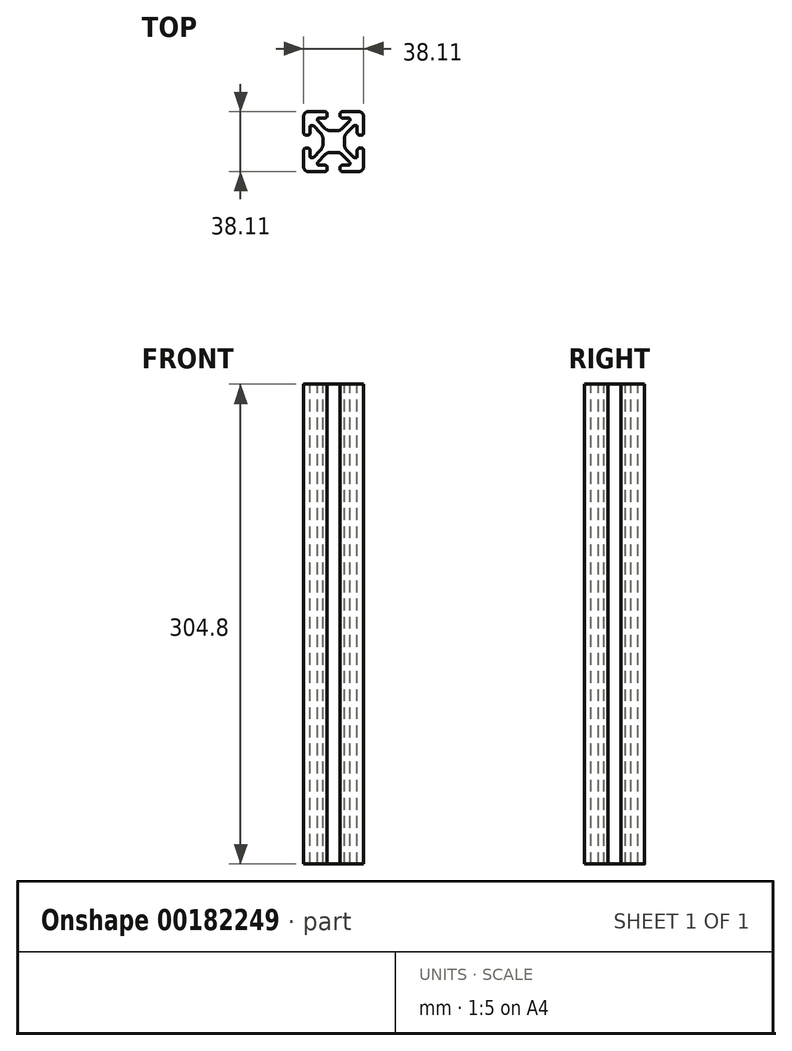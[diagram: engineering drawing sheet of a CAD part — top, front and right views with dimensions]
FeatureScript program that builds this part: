
annotation { "Feature Type Name" : "Feature", "Feature Type Description" : "" }
export const myFeature = defineFeature(function(context is Context, id is Id, definition is map)
    precondition{}
    {
        {
            var Q0;
            Q0=qCreatedBy(makeId("Top.planeOp"),FACE);
            var sketch = newSketch(context, id + "F0", { "sketchPlane" : qUnion([Q0])});
            skLineSegment(sketch, "E0.0", {"start": v(-3.18, 31.75) * mm, "end": v(-3.18, 21.51) * mm});
            skArc(sketch, "E1.0", {"start": v(0, 34.93) * mm, "mid": v(-2.25, 34) * mm, "end": v(-3.18, 31.75) * mm});
            skArc(sketch, "E2.0", {"start": v(-3.18, 21.51) * mm, "mid": v(-2.71, 20.4) * mm, "end": v(-1.6, 19.94) * mm});
            skLineSegment(sketch, "E3.0", {"start": v(-1.6, 19.94) * mm, "end": v(-0.69, 19.94) * mm});
            skArc(sketch, "E4.0", {"start": v(-0.69, 19.94) * mm, "mid": v(0.43, 20.4) * mm, "end": v(0.89, 21.51) * mm});
            skLineSegment(sketch, "E5.0", {"start": v(0.89, 21.51) * mm, "end": v(0.89, 25.27) * mm});
            skArc(sketch, "E6.0", {"start": v(0.89, 25.27) * mm, "mid": v(1.15, 25.9) * mm, "end": v(1.78, 26.16) * mm});
            skLineSegment(sketch, "E7.0", {"start": v(1.78, 26.16) * mm, "end": v(2.35, 26.16) * mm});
            skArc(sketch, "E8.0", {"start": v(2.35, 26.16) * mm, "mid": v(2.69, 26.1) * mm, "end": v(2.97, 25.9) * mm});
            skLineSegment(sketch, "E9.0", {"start": v(2.97, 25.9) * mm, "end": v(7.61, 21.26) * mm});
            skArc(sketch, "E10.0", {"start": v(7.61, 21.26) * mm, "mid": v(8.64, 19.72) * mm, "end": v(9, 17.9) * mm});
            skLineSegment(sketch, "E11.0", {"start": v(9, 17.9) * mm, "end": v(9, 13.85) * mm});
            skArc(sketch, "E12.0", {"start": v(9, 13.85) * mm, "mid": v(8.64, 12.03) * mm, "end": v(7.61, 10.49) * mm});
            skLineSegment(sketch, "E13.0", {"start": v(7.61, 10.49) * mm, "end": v(2.97, 5.85) * mm});
            skArc(sketch, "E14.0", {"start": v(2.97, 5.85) * mm, "mid": v(2.69, 5.66) * mm, "end": v(2.35, 5.59) * mm});
            skLineSegment(sketch, "E15.0", {"start": v(2.35, 5.59) * mm, "end": v(1.78, 5.59) * mm});
            skArc(sketch, "E16.0", {"start": v(1.78, 5.59) * mm, "mid": v(1.15, 5.85) * mm, "end": v(0.89, 6.48) * mm});
            skLineSegment(sketch, "E17.0", {"start": v(0.89, 6.48) * mm, "end": v(0.89, 10.24) * mm});
            skArc(sketch, "E18.0", {"start": v(0.89, 10.24) * mm, "mid": v(0.43, 11.35) * mm, "end": v(-0.69, 11.81) * mm});
            skLineSegment(sketch, "E19.0", {"start": v(-0.69, 11.81) * mm, "end": v(-1.6, 11.81) * mm});
            skArc(sketch, "E20.0", {"start": v(-1.6, 11.81) * mm, "mid": v(-2.71, 11.35) * mm, "end": v(-3.17, 10.24) * mm});
            skLineSegment(sketch, "E21.0", {"start": v(-3.17, 10.24) * mm, "end": v(-3.17, 0) * mm});
            skArc(sketch, "E22.0", {"start": v(-3.17, 0) * mm, "mid": v(-2.25, -2.25) * mm, "end": v(0, -3.17) * mm});
            skLineSegment(sketch, "E23.0", {"start": v(0, -3.17) * mm, "end": v(10.24, -3.17) * mm});
            skArc(sketch, "E24.0", {"start": v(10.24, -3.17) * mm, "mid": v(11.35, -2.71) * mm, "end": v(11.81, -1.6) * mm});
            skLineSegment(sketch, "E25.0", {"start": v(11.81, -1.6) * mm, "end": v(11.81, -0.69) * mm});
            skArc(sketch, "E26.0", {"start": v(11.81, -0.69) * mm, "mid": v(11.35, 0.43) * mm, "end": v(10.24, 0.89) * mm});
            skLineSegment(sketch, "E27.0", {"start": v(10.24, 0.89) * mm, "end": v(6.48, 0.89) * mm});
            skArc(sketch, "E28.0", {"start": v(6.48, 0.89) * mm, "mid": v(5.85, 1.15) * mm, "end": v(5.59, 1.78) * mm});
            skLineSegment(sketch, "E29.0", {"start": v(5.59, 1.78) * mm, "end": v(5.59, 2.35) * mm});
            skArc(sketch, "E30.0", {"start": v(5.59, 2.35) * mm, "mid": v(5.66, 2.69) * mm, "end": v(5.85, 2.97) * mm});
            skLineSegment(sketch, "E31.0", {"start": v(5.85, 2.97) * mm, "end": v(10.49, 7.61) * mm});
            skArc(sketch, "E32.0", {"start": v(10.49, 7.61) * mm, "mid": v(12.03, 8.64) * mm, "end": v(13.85, 9) * mm});
            skLineSegment(sketch, "E33.0", {"start": v(13.85, 9) * mm, "end": v(17.9, 9) * mm});
            skArc(sketch, "E34.0", {"start": v(17.9, 9) * mm, "mid": v(19.72, 8.64) * mm, "end": v(21.26, 7.61) * mm});
            skLineSegment(sketch, "E35.0", {"start": v(21.26, 7.61) * mm, "end": v(25.9, 2.97) * mm});
            skArc(sketch, "E36.0", {"start": v(25.9, 2.97) * mm, "mid": v(26.1, 2.69) * mm, "end": v(26.16, 2.35) * mm});
            skPoint(sketch, "E37.0", {"position": v(26.16, 1.78) * mm});
            skArc(sketch, "E38.0", {"start": v(26.16, 1.78) * mm, "mid": v(25.9, 1.15) * mm, "end": v(25.27, 0.89) * mm});
            skLineSegment(sketch, "E39.0", {"start": v(25.27, 0.89) * mm, "end": v(21.51, 0.89) * mm});
            skArc(sketch, "E40.0", {"start": v(21.51, 0.89) * mm, "mid": v(20.4, 0.43) * mm, "end": v(19.94, -0.69) * mm});
            skPoint(sketch, "E41.0", {"position": v(19.94, -1.6) * mm});
            skLineSegment(sketch, "E42.0", {"start": v(19.94, -0.69) * mm, "end": v(19.94, -1.6) * mm});
            skArc(sketch, "E43.0", {"start": v(19.94, -1.6) * mm, "mid": v(20.4, -2.71) * mm, "end": v(21.51, -3.17) * mm});
            skLineSegment(sketch, "E44.0", {"start": v(21.51, -3.17) * mm, "end": v(31.75, -3.17) * mm});
            skArc(sketch, "E45.0", {"start": v(31.75, -3.17) * mm, "mid": v(34, -2.25) * mm, "end": v(34.93, 0) * mm});
            skLineSegment(sketch, "E46.0", {"start": v(34.93, 0) * mm, "end": v(34.93, 10.24) * mm});
            skArc(sketch, "E47.0", {"start": v(34.93, 10.24) * mm, "mid": v(34.46, 11.35) * mm, "end": v(33.35, 11.81) * mm});
            skLineSegment(sketch, "E48.0", {"start": v(33.35, 11.81) * mm, "end": v(32.44, 11.81) * mm});
            skArc(sketch, "E49.0", {"start": v(32.44, 11.81) * mm, "mid": v(31.32, 11.35) * mm, "end": v(30.86, 10.24) * mm});
            skLineSegment(sketch, "E50.0", {"start": v(30.86, 10.24) * mm, "end": v(30.86, 6.48) * mm});
            skArc(sketch, "E51.0", {"start": v(30.86, 6.48) * mm, "mid": v(30.6, 5.85) * mm, "end": v(29.97, 5.59) * mm});
            skLineSegment(sketch, "E52.0", {"start": v(29.97, 5.59) * mm, "end": v(29.4, 5.59) * mm});
            skArc(sketch, "E53.0", {"start": v(29.4, 5.59) * mm, "mid": v(29.06, 5.66) * mm, "end": v(28.78, 5.85) * mm});
            skLineSegment(sketch, "E54.0", {"start": v(28.78, 5.85) * mm, "end": v(24.14, 10.49) * mm});
            skArc(sketch, "E55.0", {"start": v(24.14, 10.49) * mm, "mid": v(23.1, 12.03) * mm, "end": v(22.74, 13.85) * mm});
            skLineSegment(sketch, "E56.0", {"start": v(22.74, 13.85) * mm, "end": v(22.74, 17.9) * mm});
            skArc(sketch, "E57.0", {"start": v(22.74, 17.9) * mm, "mid": v(23.1, 19.72) * mm, "end": v(24.14, 21.26) * mm});
            skLineSegment(sketch, "E58.0", {"start": v(24.14, 21.26) * mm, "end": v(28.78, 25.9) * mm});
            skArc(sketch, "E59.0", {"start": v(28.78, 25.9) * mm, "mid": v(29.06, 26.1) * mm, "end": v(29.4, 26.16) * mm});
            skLineSegment(sketch, "E60.0", {"start": v(29.4, 26.16) * mm, "end": v(29.97, 26.16) * mm});
            skArc(sketch, "E61.0", {"start": v(29.97, 26.16) * mm, "mid": v(30.6, 25.9) * mm, "end": v(30.86, 25.27) * mm});
            skLineSegment(sketch, "E62.0", {"start": v(30.86, 25.27) * mm, "end": v(30.86, 21.51) * mm});
            skArc(sketch, "E63.0", {"start": v(30.86, 21.51) * mm, "mid": v(31.32, 20.4) * mm, "end": v(32.44, 19.94) * mm});
            skLineSegment(sketch, "E64.0", {"start": v(32.44, 19.94) * mm, "end": v(33.35, 19.94) * mm});
            skArc(sketch, "E65.0", {"start": v(33.35, 19.94) * mm, "mid": v(34.46, 20.4) * mm, "end": v(34.93, 21.51) * mm});
            skLineSegment(sketch, "E66.0", {"start": v(34.93, 21.51) * mm, "end": v(34.93, 31.75) * mm});
            skArc(sketch, "E67.0", {"start": v(34.93, 31.75) * mm, "mid": v(34, 34) * mm, "end": v(31.75, 34.93) * mm});
            skLineSegment(sketch, "E68.0", {"start": v(31.75, 34.93) * mm, "end": v(21.51, 34.93) * mm});
            skArc(sketch, "E69.0", {"start": v(21.51, 34.93) * mm, "mid": v(20.4, 34.46) * mm, "end": v(19.94, 33.35) * mm});
            skLineSegment(sketch, "E70.0", {"start": v(19.94, 33.35) * mm, "end": v(19.94, 32.44) * mm});
            skArc(sketch, "E71.0", {"start": v(19.94, 32.44) * mm, "mid": v(20.4, 31.32) * mm, "end": v(21.51, 30.86) * mm});
            skLineSegment(sketch, "E72.0", {"start": v(21.51, 30.86) * mm, "end": v(25.27, 30.86) * mm});
            skArc(sketch, "E73.0", {"start": v(25.27, 30.86) * mm, "mid": v(25.9, 30.6) * mm, "end": v(26.16, 29.97) * mm});
            skLineSegment(sketch, "E74.0", {"start": v(26.16, 29.97) * mm, "end": v(26.16, 29.4) * mm});
            skArc(sketch, "E75.0", {"start": v(26.16, 29.4) * mm, "mid": v(26.1, 29.06) * mm, "end": v(25.9, 28.78) * mm});
            skLineSegment(sketch, "E76.0", {"start": v(25.9, 28.78) * mm, "end": v(21.26, 24.14) * mm});
            skArc(sketch, "E77.0", {"start": v(11.81, 33.35) * mm, "mid": v(11.35, 34.46) * mm, "end": v(10.24, 34.93) * mm});
            skLineSegment(sketch, "E78.0", {"start": v(11.81, 32.44) * mm, "end": v(11.81, 33.35) * mm});
            skArc(sketch, "E79.0", {"start": v(10.24, 30.86) * mm, "mid": v(11.35, 31.32) * mm, "end": v(11.81, 32.44) * mm});
            skLineSegment(sketch, "E80.0", {"start": v(6.48, 30.86) * mm, "end": v(10.24, 30.86) * mm});
            skArc(sketch, "E81.0", {"start": v(5.59, 29.97) * mm, "mid": v(5.85, 30.6) * mm, "end": v(6.48, 30.86) * mm});
            skLineSegment(sketch, "E82.0", {"start": v(5.59, 29.4) * mm, "end": v(5.59, 29.97) * mm});
            skArc(sketch, "E83.0", {"start": v(5.85, 28.78) * mm, "mid": v(5.66, 29.06) * mm, "end": v(5.59, 29.4) * mm});
            skLineSegment(sketch, "E84.0", {"start": v(10.49, 24.14) * mm, "end": v(5.85, 28.78) * mm});
            skArc(sketch, "E85.0", {"start": v(13.85, 22.74) * mm, "mid": v(12.03, 23.1) * mm, "end": v(10.49, 24.14) * mm});
            skLineSegment(sketch, "E86.0", {"start": v(17.9, 22.74) * mm, "end": v(13.85, 22.74) * mm});
            skArc(sketch, "E87.0", {"start": v(21.26, 24.14) * mm, "mid": v(19.72, 23.1) * mm, "end": v(17.9, 22.74) * mm});
            skLineSegment(sketch, "E88.0", {"start": v(26.16, 2.35) * mm, "end": v(26.16, 1.78) * mm});
            skLineSegment(sketch, "E89", {"start": v(0, 34.93) * mm, "end": v(10.24, 34.93) * mm});
            skSolve(sketch);
        }
        {
            var Q0;
            Q0=qSketchRegion(id+"F0",true);
            extrude(context, id + "F1", {"entities" : qUnion([Q0]), "oppositeDirection" : true, "depth" : 304.8 * mm});
        }
    });
